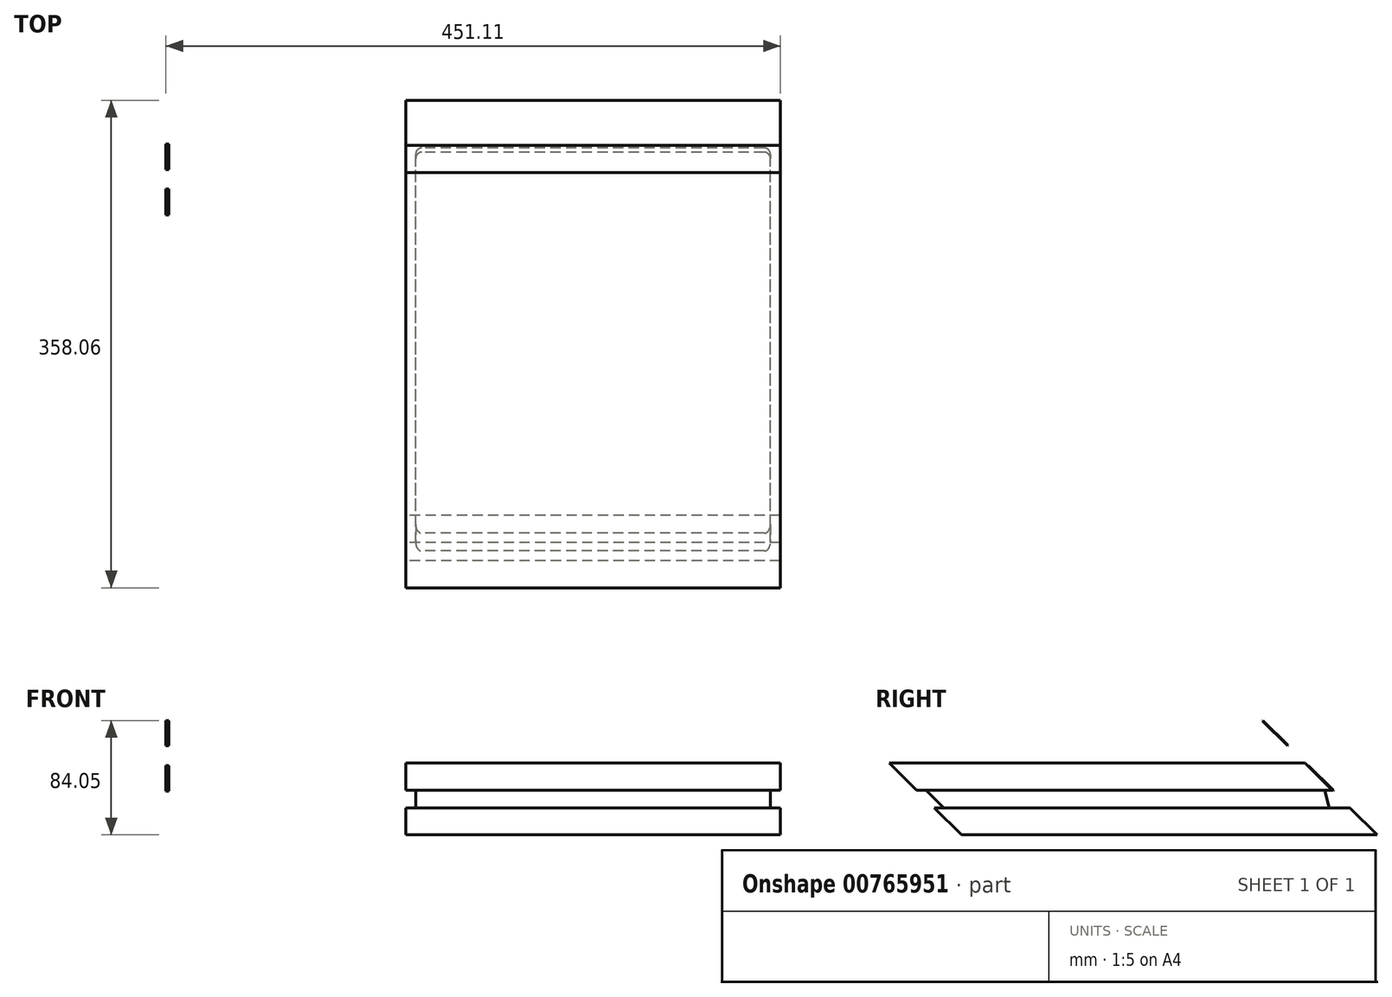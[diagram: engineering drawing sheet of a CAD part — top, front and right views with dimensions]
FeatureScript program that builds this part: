
annotation { "Feature Type Name" : "Feature", "Feature Type Description" : "" }
export const myFeature = defineFeature(function(context is Context, id is Id, definition is map)
    precondition{}
    {
        {
            var Q0;
            Q0=qCreatedBy(makeId("Right.planeOp"),FACE);
            var sketch = newSketch(context, id + "F0", { "sketchPlane" : qUnion([Q0])});
            skLineSegment(sketch, "E0", {"start": v(-144.56, 76.43) * mm, "end": v(160.44, 76.43) * mm});
            skLineSegment(sketch, "E1", {"start": v(140.44, 96.34) * mm, "end": v(140.44, 76.43) * mm, "construction": true});
            skLineSegment(sketch, "E2", {"start": v(140.44, 96.34) * mm, "end": v(-164.56, 96.34) * mm});
            skLineSegment(sketch, "E3", {"start": v(-164.56, 96.34) * mm, "end": v(-144.56, 76.43) * mm});
            skLineSegment(sketch, "E4", {"start": v(140.44, 96.34) * mm, "end": v(160.44, 76.43) * mm});
            skSolve(sketch);
        }
        {
            var Q0;
            Q0=qCreatedBy(makeId("Right.planeOp"),FACE);
            var sketch = newSketch(context, id + "F1", { "sketchPlane" : qUnion([Q0])});
            skLineSegment(sketch, "E5", {"start": v(-164.56, 96.34) * mm, "end": v(-157.56, 96.34) * mm});
            skLineSegment(sketch, "E6", {"start": v(-157.56, 96.34) * mm, "end": v(-170.62, 109.34) * mm});
            skLineSegment(sketch, "E7", {"start": v(140.44, 96.34) * mm, "end": v(125.44, 96.34) * mm, "construction": true});
            skLineSegment(sketch, "E8", {"start": v(-157.56, 96.34) * mm, "end": v(125.44, 96.34) * mm});
            skLineSegment(sketch, "E9", {"start": v(125.44, 96.34) * mm, "end": v(122.28, 109.34) * mm});
            skLineSegment(sketch, "E10", {"start": v(-170.62, 109.34) * mm, "end": v(122.28, 109.34) * mm});
            skSolve(sketch);
        }
        {
            var Q0;
            Q0=qCreatedBy(makeId("Right.planeOp"),FACE);
            var sketch = newSketch(context, id + "F2", { "sketchPlane" : qUnion([Q0])});
            skLineSegment(sketch, "E11", {"start": v(-177.62, 109.34) * mm, "end": v(-197.62, 129.26) * mm});
            skLineSegment(sketch, "E12", {"start": v(127.38, 109.34) * mm, "end": v(107.38, 129.26) * mm});
            skLineSegment(sketch, "E13", {"start": v(-164.56, 96.34) * mm, "end": v(-177.62, 109.34) * mm, "construction": true});
            skLineSegment(sketch, "E14", {"start": v(140.44, 96.34) * mm, "end": v(127.38, 109.34) * mm, "construction": true});
            skLineSegment(sketch, "E15", {"start": v(-177.62, 109.34) * mm, "end": v(127.38, 109.34) * mm});
            skLineSegment(sketch, "E16", {"start": v(-197.62, 129.26) * mm, "end": v(107.38, 129.26) * mm});
            skSolve(sketch);
        }
        {
            var Q0;
            Q0 = qSketchRegion(id + "F0", true);
            extrude(context, id + "F3", {"entities" : qUnion([Q0]), "depth" : 275 * mm, "offsetDistance" : 25 * mm});
        }
        {
            var Q0;
            Q0 = qSketchRegion(id + "F1", true);
            extrude(context, id + "F4", {"entities" : qUnion([Q0]), "depth" : 267.7 * mm, "offsetDistance" : 25 * mm, "hasSecondDirection" : true, "secondDirectionOppositeDirection" : false, "secondDirectionDepth" : 7.3 * mm});
        }
        {
            var Q0;
            Q0 = qSketchRegion(id + "F2", true);
            extrude(context, id + "F5", {"entities" : qUnion([Q0]), "depth" : 275 * mm, "offsetDistance" : 25 * mm});
        }
        {
            var Q0;
            Q0=makeQuery(id+"F3.opExtrude","SWEPT_EDGE",EDGE,{"disambiguationData":[OSD([sQuery(id+"F0.wireOp",EDGE,"E2"),sQuery(id+"F0.wireOp",EDGE,"E4")])]});
            fillet(context, id + "F6", {"entities" : qUnion([Q0]), "radius" : 1 * mm, "tangentPropagation" : true, "allowEdgeOverflow" : false});
        }
        {
            var Q0;
            Q0=makeQuery(id+"F4.opExtrude","CAP_EDGE",EDGE,{"disambiguationData":[OSD([sQuery(id+"F1.wireOp",EDGE,"E9")])],"isStart":false});
            var Q1;
            Q1=makeQuery(id+"F4.opExtrude","CAP_EDGE",EDGE,{"disambiguationData":[OSD([sQuery(id+"F1.wireOp",EDGE,"E9")])],"isStart":true});
            var Q2;
            Q2=makeQuery(id+"F4.opExtrude","CAP_EDGE",EDGE,{"disambiguationData":[OSD([sQuery(id+"F1.wireOp",EDGE,"E6")])],"isStart":false});
            var Q3;
            Q3=makeQuery(id+"F4.opExtrude","CAP_EDGE",EDGE,{"disambiguationData":[OSD([sQuery(id+"F1.wireOp",EDGE,"E6")])],"isStart":true});
            fillet(context, id + "F7", {"entities" : qUnion([Q0, Q1, Q2, Q3]), "radius" : 4.5 * mm, "tangentPropagation" : true, "allowEdgeOverflow" : false});
        }
        {
            var Q0;
            Q0=makeQuery(id+"F5.opExtrude","SWEPT_FACE",FACE,{"disambiguationData":[OSD([sQuery(id+"F2.wireOp",EDGE,"E12")])]});
            var sketch = newSketch(context, id + "F8", { "sketchPlane" : qUnion([Q0])});
            skLineSegment(sketch, "E17.bottom", {"start": v(174.1, 12) * mm, "end": v(176.1, 12) * mm});
            skLineSegment(sketch, "E17.top", {"start": v(174.1, -14) * mm, "end": v(176.1, -14) * mm});
            skLineSegment(sketch, "E17.left", {"start": v(174.1, 12) * mm, "end": v(174.1, -14) * mm});
            skLineSegment(sketch, "E17.right", {"start": v(176.1, 12) * mm, "end": v(176.1, -14) * mm});
            skPoint(sketch, "E17.middle", {"position": v(175.1, -1) * mm});
            skSolve(sketch);
        }
        {
            var Q0;
            Q0 = qSketchRegion(id + "F8", true);
            extrude(context, id + "F9", {"entities" : qUnion([Q0]), "operationType" : NewBodyOperationType.ADD, "depth" : 0.5 * mm, "offsetDistance" : 25 * mm});
        }
        {
            var Q0;
            Q0=makeQuery(id+"F3.opExtrude","SWEPT_FACE",FACE,{"disambiguationData":[OSD([sQuery(id+"F0.wireOp",EDGE,"E4")])]});
            var sketch = newSketch(context, id + "F10", { "sketchPlane" : qUnion([Q0])});
            skSolve(sketch);
        }
        {
            var Q0;
            {var subQ0=sQuery(id+"F0.wireOp",EDGE,"E4");Q0=makeQuery(id+"F10.imprint","IMPRINT",FACE,{"disambiguationData":[TD([[makeQuery(id+"F10.imprint","IMPRINT",EDGE,{"derivedFrom":makeQuery(id+"F3.opExtrude","CAP_EDGE",EDGE,{"disambiguationData":[OSD([subQ0])],"isStart":true})}),-1.0]])]});}
            var sketch = newSketch(context, id + "F11", { "sketchPlane" : qUnion([Q0])});
            skLineSegment(sketch, "E18", {"start": v(175.1, 45.86) * mm, "end": v(275, 45.86) * mm, "construction": true});
            skLineSegment(sketch, "E19.bottom", {"start": v(174.1, 58.86) * mm, "end": v(176.1, 58.86) * mm});
            skLineSegment(sketch, "E19.top", {"start": v(174.1, 32.86) * mm, "end": v(176.1, 32.86) * mm});
            skLineSegment(sketch, "E19.left", {"start": v(174.1, 58.86) * mm, "end": v(174.1, 32.86) * mm});
            skLineSegment(sketch, "E19.right", {"start": v(176.1, 58.86) * mm, "end": v(176.1, 32.86) * mm});
            skPoint(sketch, "E19.middle", {"position": v(175.1, 45.86) * mm});
            skSolve(sketch);
        }
        {
            var Q0;
            Q0 = qSketchRegion(id + "F11", true);
            extrude(context, id + "F12", {"entities" : qUnion([Q0]), "operationType" : NewBodyOperationType.ADD, "depth" : 0.5 * mm, "offsetDistance" : 25 * mm});
        }
    });
